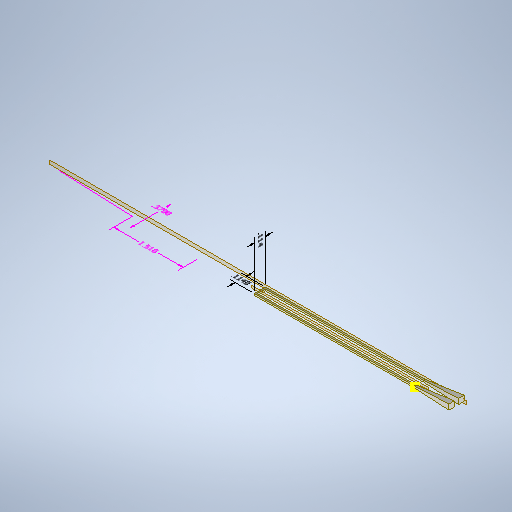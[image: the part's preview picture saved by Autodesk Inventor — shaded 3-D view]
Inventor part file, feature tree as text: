
AUTODESK INVENTOR PART (.ipt)
format: ipt  version: 2025.2 (Build 292293000, 293)  size: 307,712 bytes
history: native  units: in
note: dims shown in document units (in); Inventor stores cm internally (conversion verified against a paired STEP export)
features: other x6, plane x4, sketch x4, sweep x1, loft x1, mirror x1, projected_geometry x1
ambient origin geometry x8: Origin, YZ Plane, XZ Plane, XY Plane, X Axis, Y Axis, Z Axis, Center Point
bodies: Solid1 (feature_tree)
feature tree (18):
  other  "Annotations"
  sweep  "Sweep1"
  plane  "Work Plane1"
  plane  "Work Plane2"
  plane  "Work Plane4"
  sketch  "Sketch15"  dims[d86=-0.1175in]
  sketch  "Sketch16"  dims[d89=0.1in d90=0.0in d91=0.0in d92=0.0in d98=0.017in d99=0.017in d100=0.055in d102=0.055in d104=0.0in d109=0.0in d110=90.0deg d111=0.0in d112=90.0deg d116=-0.057in d113=0.0in d114=0.3937in d115=0.114in d117=0.0226in d118=0.3734in d119=0.114in d42=0.2341in d43=0.169in d44=0.37in d48=0.2141in d49=0.2512in d50=1.51in]
  loft  "Loft3"
  plane  "Work Plane5"
  mirror  "Mirror3"
  sketch  "Sketch1"  dims[d6=0.0in d7=0.0in d11=0.375in d19=-0.25in]
  sketch  "Sketch2"  dims[d69=1.625in d70=1.625in]
  projected_geometry  "Projected Loop1"
  other  "Edges4"
  other  "Linear Dimension 1"
  other  "Linear Dimension 3"
  other  "Linear Dimension 4"
  other  "Linear Dimension 5"
